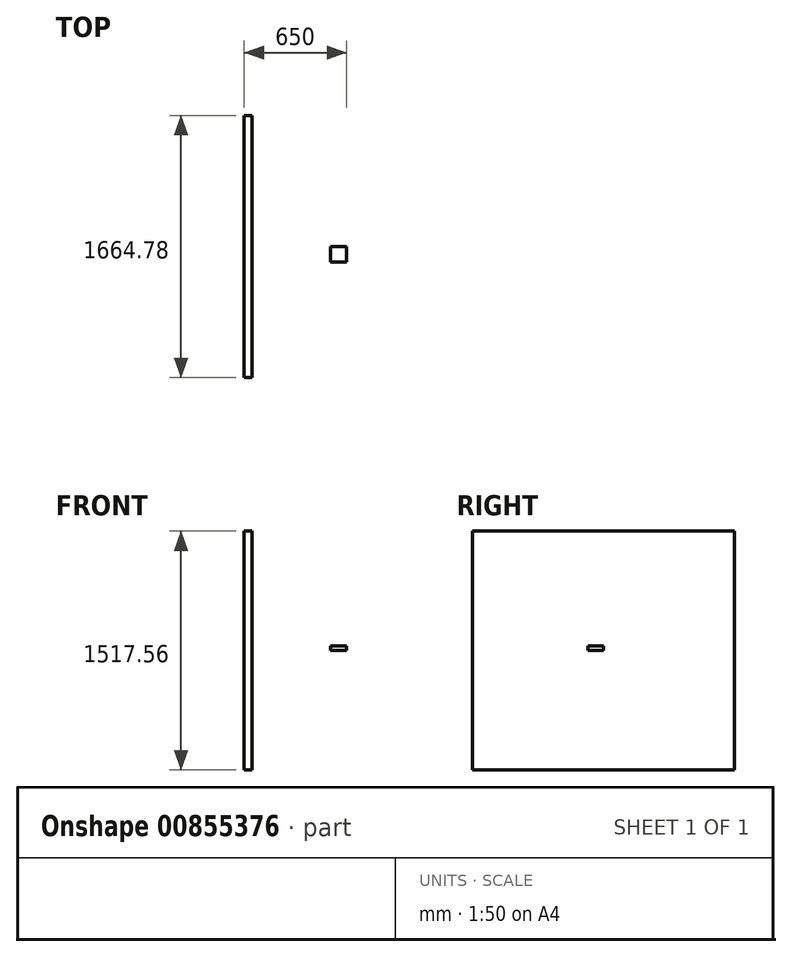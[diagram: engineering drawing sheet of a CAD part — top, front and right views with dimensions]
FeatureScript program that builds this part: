
annotation { "Feature Type Name" : "Feature", "Feature Type Description" : "" }
export const myFeature = defineFeature(function(context is Context, id is Id, definition is map)
    precondition{}
    {
        {
            var Q0;
            Q0=qCreatedBy(makeId("Right.planeOp"),FACE);
            var sketch = newSketch(context, id + "F0", { "sketchPlane" : qUnion([Q0])});
            skLineSegment(sketch, "E0.bottom", {"start": v(832.39, 758.78) * mm, "end": v(-832.39, 758.78) * mm});
            skLineSegment(sketch, "E0.top", {"start": v(832.39, -758.78) * mm, "end": v(-832.39, -758.78) * mm});
            skLineSegment(sketch, "E0.left", {"start": v(832.39, 758.78) * mm, "end": v(832.39, -758.78) * mm});
            skLineSegment(sketch, "E0.right", {"start": v(-832.39, 758.78) * mm, "end": v(-832.39, -758.78) * mm});
            skPoint(sketch, "E0.middle", {"position": v(0, 0) * mm});
            skSolve(sketch);
        }
        {
            var Q0;
            Q0 = qSketchRegion(id + "F0", true);
            extrude(context, id + "F1", {"entities" : qUnion([Q0]), "depth" : 50 * mm, "offsetDistance" : 25 * mm});
        }
        {
            var Q0;
            Q0=qCreatedBy(makeId("Front.planeOp"),FACE);
            var sketch = newSketch(context, id + "F2", { "sketchPlane" : qUnion([Q0])});
            skLineSegment(sketch, "E1.bottom", {"start": v(550, 0) * mm, "end": v(650, 0) * mm});
            skLineSegment(sketch, "E1.top", {"start": v(550, 30) * mm, "end": v(650, 30) * mm});
            skLineSegment(sketch, "E1.left", {"start": v(550, 0) * mm, "end": v(550, 30) * mm});
            skLineSegment(sketch, "E1.right", {"start": v(650, 0) * mm, "end": v(650, 30) * mm});
            skSolve(sketch);
        }
        {
            var Q0;
            Q0 = qSketchRegion(id + "F2", true);
            extrude(context, id + "F3", {"entities" : qUnion([Q0]), "depth" : 100 * mm, "offsetDistance" : 25 * mm});
        }
    });
